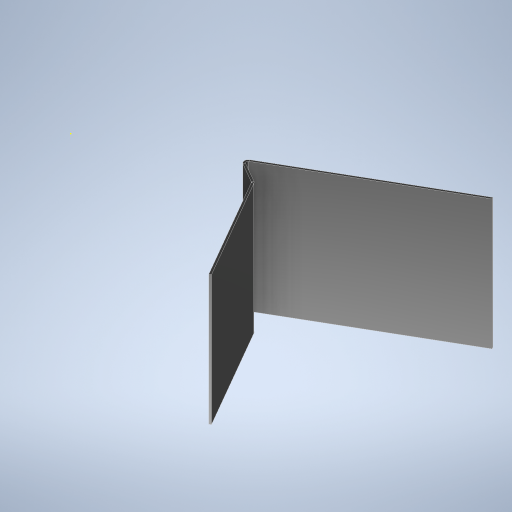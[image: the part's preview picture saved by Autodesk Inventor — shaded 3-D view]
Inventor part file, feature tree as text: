
AUTODESK INVENTOR PART (.ipt)
format: ipt  version: 2024 (Build 280153000, 153)  size: 293,888 bytes
history: native  units: mm
features: sheet_metal_op x3, other x2, sketch x1
ambient origin geometry x8: Origin, YZ Plane, XZ Plane, XY Plane, X Axis, Y Axis, Z Axis, Center Point
bodies: Solid1 (feature_tree)
feature tree (6):
  sheet_metal_op  "Face1"
  sheet_metal_op  "Fold1"
  sheet_metal_op  "Fold2"
  other  "Plate1"
  sketch  "Sketch2"  dims[d0=500.0mm d1=200.0mm d2=3.048mm d3=180.0mm d4=20.0mm d5=3.048mm d6=1.524mm d7=6.096mm d8=3.048mm d9=30.0deg d10=3.048mm d11=40.0mm d12=3.048mm d13=1.524mm d14=6.096mm d15=3.048mm d16=120.0deg d17=3.048mm]
  other  "Definition1"
